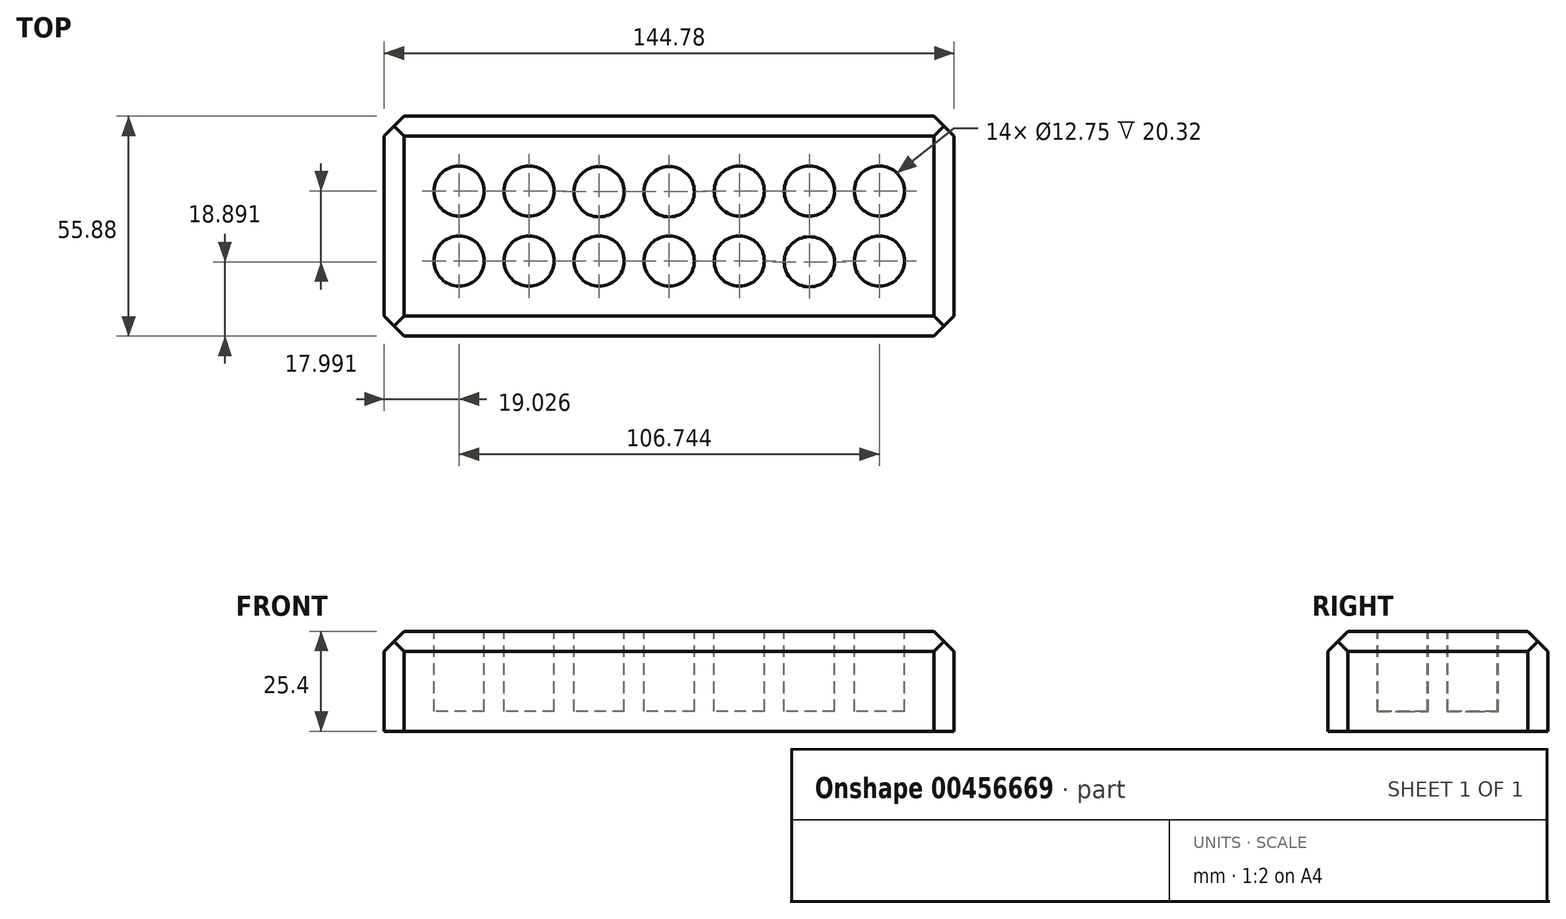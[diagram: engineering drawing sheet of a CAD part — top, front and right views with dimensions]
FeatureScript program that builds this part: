
annotation { "Feature Type Name" : "Feature", "Feature Type Description" : "" }
export const myFeature = defineFeature(function(context is Context, id is Id, definition is map)
    precondition{}
    {
        {
            var Q0;
            Q0=qCreatedBy(makeId("Top.planeOp"),FACE);
            var sketch = newSketch(context, id + "F0", { "sketchPlane" : qUnion([Q0])});
            skLineSegment(sketch, "E0.bottom", {"start": v(0, 0) * mm, "end": v(144.78, 0) * mm});
            skLineSegment(sketch, "E0.top", {"start": v(0, -55.88) * mm, "end": v(144.78, -55.88) * mm});
            skLineSegment(sketch, "E0.left", {"start": v(0, 0) * mm, "end": v(0, -55.88) * mm});
            skLineSegment(sketch, "E0.right", {"start": v(144.78, 0) * mm, "end": v(144.78, -55.88) * mm});
            skSolve(sketch);
        }
        {
            var Q0;
            Q0=makeQuery(id+"F0.imprint","IMPRINT",FACE,{"disambiguationData":[TD([[makeQuery(id+"F0.imprint","IMPRINT",EDGE,{"derivedFrom":sQuery(id+"F0.wireOp",EDGE,"E0.bottom")}),-1.0]])]});
            extrude(context, id + "F1", {"entities" : qUnion([Q0]), "depth" : 25.4 * mm});
        }
        {
            var Q0;
            Q0=makeQuery(id+"F1.opExtrude","CAP_FACE",FACE,{"disambiguationData":[OSD([sQuery(id+"F0.wireOp",EDGE,"E0.bottom"),sQuery(id+"F0.wireOp",EDGE,"E0.top"),sQuery(id+"F0.wireOp",EDGE,"E0.left"),sQuery(id+"F0.wireOp",EDGE,"E0.right")])],"isStart":false});
            var sketch = newSketch(context, id + "F2", { "sketchPlane" : qUnion([Q0])});
            skCircle(sketch, "E1", {"center": v(19.03, -19) * mm, "radius": 6.37 * mm});
            skCircle(sketch, "E2", {"center": v(36.82, -19) * mm, "radius": 6.37 * mm});
            skCircle(sketch, "E3", {"center": v(54.6, -19.2) * mm, "radius": 6.37 * mm});
            skCircle(sketch, "E4", {"center": v(72.4, -19.2) * mm, "radius": 6.37 * mm});
            skCircle(sketch, "E5", {"center": v(90.19, -19) * mm, "radius": 6.37 * mm});
            skCircle(sketch, "E6", {"center": v(107.98, -19) * mm, "radius": 6.37 * mm});
            skCircle(sketch, "E7", {"center": v(125.77, -19) * mm, "radius": 6.37 * mm});
            skCircle(sketch, "E8", {"center": v(19.03, -36.79) * mm, "radius": 6.37 * mm});
            skCircle(sketch, "E9", {"center": v(36.82, -36.79) * mm, "radius": 6.37 * mm});
            skCircle(sketch, "E10", {"center": v(54.6, -36.79) * mm, "radius": 6.37 * mm});
            skCircle(sketch, "E11", {"center": v(72.4, -36.79) * mm, "radius": 6.37 * mm});
            skCircle(sketch, "E12", {"center": v(90.19, -36.79) * mm, "radius": 6.37 * mm});
            skCircle(sketch, "E13", {"center": v(107.98, -36.99) * mm, "radius": 6.37 * mm});
            skCircle(sketch, "E14", {"center": v(125.77, -36.79) * mm, "radius": 6.37 * mm});
            skSolve(sketch);
        }
        {
            var Q0;
            Q0=makeQuery(id+"F2.imprint","IMPRINT",FACE,{"disambiguationData":[TD([[makeQuery(id+"F2.imprint","IMPRINT",EDGE,{"derivedFrom":sQuery(id+"F2.wireOp",EDGE,"E7")}),1.0]])]});
            var Q1;
            Q1=makeQuery(id+"F2.imprint","IMPRINT",FACE,{"disambiguationData":[TD([[makeQuery(id+"F2.imprint","IMPRINT",EDGE,{"derivedFrom":sQuery(id+"F2.wireOp",EDGE,"E14")}),1.0]])]});
            var Q2;
            Q2=makeQuery(id+"F2.imprint","IMPRINT",FACE,{"disambiguationData":[TD([[makeQuery(id+"F2.imprint","IMPRINT",EDGE,{"derivedFrom":sQuery(id+"F2.wireOp",EDGE,"E13")}),1.0]])]});
            var Q3;
            Q3=makeQuery(id+"F2.imprint","IMPRINT",FACE,{"disambiguationData":[TD([[makeQuery(id+"F2.imprint","IMPRINT",EDGE,{"derivedFrom":sQuery(id+"F2.wireOp",EDGE,"E6")}),1.0]])]});
            var Q4;
            Q4=makeQuery(id+"F2.imprint","IMPRINT",FACE,{"disambiguationData":[TD([[makeQuery(id+"F2.imprint","IMPRINT",EDGE,{"derivedFrom":sQuery(id+"F2.wireOp",EDGE,"E5")}),1.0]])]});
            var Q5;
            Q5=makeQuery(id+"F2.imprint","IMPRINT",FACE,{"disambiguationData":[TD([[makeQuery(id+"F2.imprint","IMPRINT",EDGE,{"derivedFrom":sQuery(id+"F2.wireOp",EDGE,"E12")}),1.0]])]});
            var Q6;
            Q6=makeQuery(id+"F2.imprint","IMPRINT",FACE,{"disambiguationData":[TD([[makeQuery(id+"F2.imprint","IMPRINT",EDGE,{"derivedFrom":sQuery(id+"F2.wireOp",EDGE,"E11")}),1.0]])]});
            var Q7;
            Q7=makeQuery(id+"F2.imprint","IMPRINT",FACE,{"disambiguationData":[TD([[makeQuery(id+"F2.imprint","IMPRINT",EDGE,{"derivedFrom":sQuery(id+"F2.wireOp",EDGE,"E4")}),1.0]])]});
            var Q8;
            Q8=makeQuery(id+"F2.imprint","IMPRINT",FACE,{"disambiguationData":[TD([[makeQuery(id+"F2.imprint","IMPRINT",EDGE,{"derivedFrom":sQuery(id+"F2.wireOp",EDGE,"E3")}),1.0]])]});
            var Q9;
            Q9=makeQuery(id+"F2.imprint","IMPRINT",FACE,{"disambiguationData":[TD([[makeQuery(id+"F2.imprint","IMPRINT",EDGE,{"derivedFrom":sQuery(id+"F2.wireOp",EDGE,"E10")}),1.0]])]});
            var Q10;
            Q10=makeQuery(id+"F2.imprint","IMPRINT",FACE,{"disambiguationData":[TD([[makeQuery(id+"F2.imprint","IMPRINT",EDGE,{"derivedFrom":sQuery(id+"F2.wireOp",EDGE,"E9")}),1.0]])]});
            var Q11;
            Q11=makeQuery(id+"F2.imprint","IMPRINT",FACE,{"disambiguationData":[TD([[makeQuery(id+"F2.imprint","IMPRINT",EDGE,{"derivedFrom":sQuery(id+"F2.wireOp",EDGE,"E2")}),1.0]])]});
            var Q12;
            Q12=makeQuery(id+"F2.imprint","IMPRINT",FACE,{"disambiguationData":[TD([[makeQuery(id+"F2.imprint","IMPRINT",EDGE,{"derivedFrom":sQuery(id+"F2.wireOp",EDGE,"E1")}),1.0]])]});
            var Q13;
            Q13=makeQuery(id+"F2.imprint","IMPRINT",FACE,{"disambiguationData":[TD([[makeQuery(id+"F2.imprint","IMPRINT",EDGE,{"derivedFrom":sQuery(id+"F2.wireOp",EDGE,"E8")}),1.0]])]});
            extrude(context, id + "F3", {"entities" : qUnion([Q0, Q1, Q2, Q3, Q4, Q5, Q6, Q7, Q8, Q9, Q10, Q11, Q12, Q13]), "operationType" : NewBodyOperationType.REMOVE, "oppositeDirection" : true, "depth" : 20.32 * mm});
        }
        {
            var Q0;
            Q0=makeQuery(id+"F1.opExtrude","CAP_EDGE",EDGE,{"disambiguationData":[OSD([sQuery(id+"F0.wireOp",EDGE,"E0.top")])],"isStart":false});
            var Q1;
            Q1=makeQuery(id+"F1.opExtrude","CAP_EDGE",EDGE,{"disambiguationData":[OSD([sQuery(id+"F0.wireOp",EDGE,"E0.bottom")])],"isStart":false});
            var Q2;
            Q2=makeQuery(id+"F1.opExtrude","CAP_EDGE",EDGE,{"disambiguationData":[OSD([sQuery(id+"F0.wireOp",EDGE,"E0.right")])],"isStart":false});
            var Q3;
            Q3=makeQuery(id+"F1.opExtrude","CAP_EDGE",EDGE,{"disambiguationData":[OSD([sQuery(id+"F0.wireOp",EDGE,"E0.left")])],"isStart":false});
            chamfer(context, id + "F4", {"entities" : qUnion([Q0, Q1, Q2, Q3]), "width" : 5.08 * mm, "tangentPropagation" : true});
        }
        {
            var Q0;
            Q0=makeQuery(id+"F1.opExtrude","SWEPT_EDGE",EDGE,{"disambiguationData":[OSD([sQuery(id+"F0.wireOp",EDGE,"E0.top"),sQuery(id+"F0.wireOp",EDGE,"E0.right")])]});
            var Q1;
            Q1=makeQuery(id+"F1.opExtrude","SWEPT_EDGE",EDGE,{"disambiguationData":[OSD([sQuery(id+"F0.wireOp",EDGE,"E0.bottom"),sQuery(id+"F0.wireOp",EDGE,"E0.right")])]});
            var Q2;
            Q2=makeQuery(id+"F1.opExtrude","SWEPT_EDGE",EDGE,{"disambiguationData":[OSD([sQuery(id+"F0.wireOp",EDGE,"E0.top"),sQuery(id+"F0.wireOp",EDGE,"E0.left")])]});
            var Q3;
            Q3=makeQuery(id+"F1.opExtrude","SWEPT_EDGE",EDGE,{"disambiguationData":[OSD([sQuery(id+"F0.wireOp",EDGE,"E0.bottom"),sQuery(id+"F0.wireOp",EDGE,"E0.left")])]});
            chamfer(context, id + "F5", {"entities" : qUnion([Q0, Q1, Q2, Q3]), "width" : 5.08 * mm, "tangentPropagation" : true});
        }
    });
